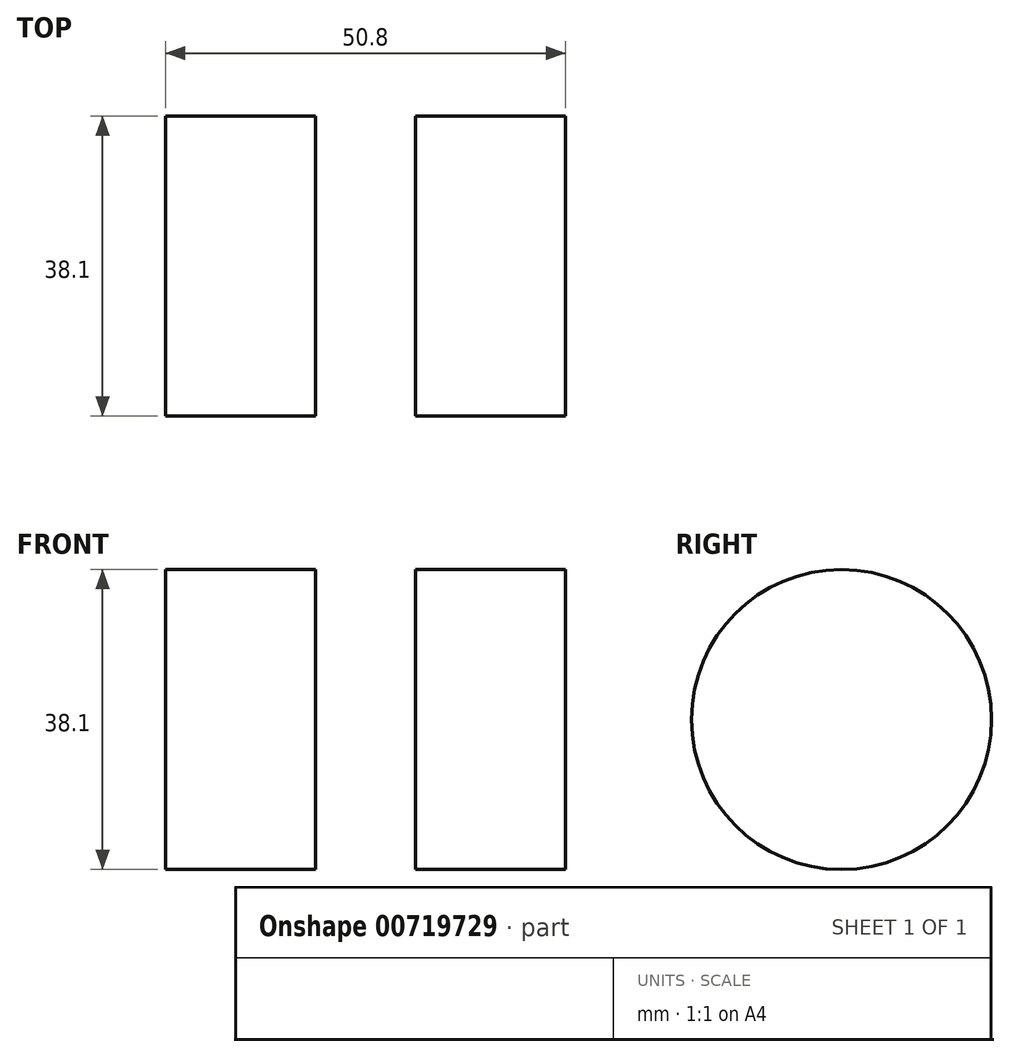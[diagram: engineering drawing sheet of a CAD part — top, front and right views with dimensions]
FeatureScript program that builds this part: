
annotation { "Feature Type Name" : "Feature", "Feature Type Description" : "" }
export const myFeature = defineFeature(function(context is Context, id is Id, definition is map)
    precondition{}
    {
        {
            var Q0;
            Q0=qCreatedBy(makeId("Front.planeOp"),FACE);
            var sketch = newSketch(context, id + "F0", { "sketchPlane" : qUnion([Q0])});
            skLineSegment(sketch, "E0.bottom", {"start": v(0, 0) * mm, "end": v(50.8, 0) * mm});
            skLineSegment(sketch, "E0.top", {"start": v(0, 25.4) * mm, "end": v(50.8, 25.4) * mm});
            skLineSegment(sketch, "E0.left", {"start": v(0, 0) * mm, "end": v(0, 25.4) * mm});
            skLineSegment(sketch, "E0.right", {"start": v(50.8, 0) * mm, "end": v(50.8, 25.4) * mm});
            skSolve(sketch);
        }
        {
            var Q0;
            Q0=makeQuery(id+"F0.imprint","IMPRINT",FACE,{"disambiguationData":[TD([[makeQuery(id+"F0.imprint","IMPRINT",EDGE,{"derivedFrom":sQuery(id+"F0.wireOp",EDGE,"E0.bottom")}),1.0]])]});
            extrude(context, id + "F1", {"entities" : qUnion([Q0]), "depth" : 1778 * mm, "offsetDistance" : 25.4 * mm});
        }
        {
            var Q0;
            Q0=makeQuery(id+"F1.opExtrude","SWEPT_FACE",FACE,{"disambiguationData":[OSD([sQuery(id+"F0.wireOp",EDGE,"E0.right")])]});
            cPlane(context, id + "F2", {"entities" : qUnion([Q0]), "cplaneType" : CPlaneType.OFFSET, "offset" : 19.05 * mm, "oppositeDirection" : true, "width" : 152.4 * mm, "height" : 152.4 * mm});
        }
        {
            var Q0;
            Q0=makeQuery(id+"F1.opExtrude","CAP_FACE",FACE,{"disambiguationData":[OSD([sQuery(id+"F0.wireOp",EDGE,"E0.bottom"),sQuery(id+"F0.wireOp",EDGE,"E0.top"),sQuery(id+"F0.wireOp",EDGE,"E0.left"),sQuery(id+"F0.wireOp",EDGE,"E0.right")])],"isStart":false});
            cPlane(context, id + "F3", {"entities" : qUnion([Q0]), "cplaneType" : CPlaneType.OFFSET, "offset" : 889 * mm, "oppositeDirection" : true, "width" : 152.4 * mm, "height" : 152.4 * mm});
        }
        {
            var Q0;
            Q0=qCreatedBy(id+"F2.planeOp",FACE);
            var sketch = newSketch(context, id + "F4", { "sketchPlane" : qUnion([Q0])});
            skPoint(sketch, "E1", {"position": v(-1791.81, 12.7) * mm});
            skCircle(sketch, "E2", {"center": v(-1791.81, 12.7) * mm, "radius": 22.23 * mm, "construction": true});
            skPoint(sketch, "E3", {"position": v(-1773.58, 25.4) * mm});
            skCircle(sketch, "E4", {"center": v(-1791.81, 12.7) * mm, "radius": 22.23 * mm});
            skCircle(sketch, "E5.MirrorC", {"center": v(13.81, 12.7) * mm, "radius": 22.23 * mm, "construction": true});
            skCircle(sketch, "E6", {"center": v(13.81, 12.7) * mm, "radius": 22.23 * mm});
            skPoint(sketch, "E7", {"position": v(-4.42, 25.4) * mm});
            skSolve(sketch);
        }
        {
            var Q0;
            Q0=makeQuery(id+"F1.opExtrude","SWEPT_FACE",FACE,{"disambiguationData":[OSD([sQuery(id+"F0.wireOp",EDGE,"E0.right")])]});
            var sketch = newSketch(context, id + "F5", { "sketchPlane" : qUnion([Q0])});
            skPoint(sketch, "E8", {"position": v(-1791.81, 12.7) * mm});
            skCircle(sketch, "E9", {"center": v(-1791.81, 12.7) * mm, "radius": 22.23 * mm});
            skCircle(sketch, "E10.MirrorC", {"center": v(13.81, 12.7) * mm, "radius": 22.23 * mm});
            skCircle(sketch, "E11", {"center": v(-1791.81, 12.7) * mm, "radius": 19.05 * mm});
            skSolve(sketch);
        }
        {
            var Q0;
            {var subQ1=sQuery(id+"F0.wireOp",EDGE,"E0.right");var subQ6=makeQuery(id+"F1.opExtrude","CAP_EDGE",EDGE,{"disambiguationData":[OSD([subQ1])],"isStart":true});Q0=makeQuery(id+"F5.imprint","IMPRINT",FACE,{"disambiguationData":[TD([[makeQuery(id+"F5.imprint","IMPRINT",EDGE,{"derivedFrom":subQ6}),-1.0]])]});}
            var Q1;
            {var subQ0=sQuery(id+"F5.wireOp",EDGE,"E9");var subQ1=sQuery(id+"F0.wireOp",EDGE,"E0.right");var subQ2=makeQuery(id+"F1.opExtrude","SWEPT_EDGE",EDGE,{"disambiguationData":[OSD([sQuery(id+"F0.wireOp",EDGE,"E0.bottom"),subQ1])]});var subQ3=makeQuery(id+"F5.imprint","INTERSECT",VERTEX,{"derivedFrom":[subQ2,subQ0]});Q1=makeQuery(id+"F5.imprint","IMPRINT",FACE,{"disambiguationData":[TD([[makeQuery(id+"F5.imprint","IMPRINT",EDGE,{"disambiguationData":[TD([[subQ3,1.0]])],"derivedFrom":subQ0}),1.0]])]});}
            extrude(context, id + "F6", {"entities" : qUnion([Q0, Q1]), "operationType" : NewBodyOperationType.ADD, "oppositeDirection" : true, "depth" : 50.8 * mm, "offsetDistance" : 25.4 * mm});
        }
        {
            var Q0;
            Q0 = qSketchRegion(id + "F4", true);
            extrude(context, id + "F7", {"entities" : qUnion([Q0]), "operationType" : NewBodyOperationType.REMOVE, "oppositeDirection" : true, "depth" : 12.7 * mm, "offsetDistance" : 25.4 * mm});
        }
        {
            var Q0;
            {var subQ0=sQuery(id+"F0.wireOp",EDGE,"E0.right");var subQ1=sQuery(id+"F0.wireOp",EDGE,"E0.top");var subQ2=sQuery(id+"F0.wireOp",EDGE,"E0.bottom");Q0=makeQuery(id+"F6.boolean.opBoolean","MERGE",FACE,{"derivedFrom":[makeQuery(id+"F1.opExtrude","SWEPT_FACE",FACE,{"disambiguationData":[OSD([subQ0])]}),makeQuery(id+"F6.opExtrude","CAP_FACE",FACE,{"disambiguationData":[OSD([subQ2,subQ1,subQ0,sQuery(id+"F5.wireOp",EDGE,"E9"),sQuery(id+"F5.wireOp",EDGE,"E11")])],"isStart":true}),makeQuery(id+"F6.opExtrude","CAP_FACE",FACE,{"disambiguationData":[OSD([subQ2,subQ1,subQ0,sQuery(id+"F5.wireOp",EDGE,"E10.MirrorC")])],"isStart":true})]});}
            var sketch = newSketch(context, id + "F8", { "sketchPlane" : qUnion([Q0])});
            skCircle(sketch, "E12", {"center": v(-1791.81, 12.7) * mm, "radius": 19.05 * mm});
            skCircle(sketch, "E13.MirrorC", {"center": v(13.81, 12.7) * mm, "radius": 19.05 * mm});
            skSolve(sketch);
        }
        {
            var Q0;
            {var subQ2=sQuery(id+"F0.wireOp",EDGE,"E0.right");Q0=makeQuery(id+"F8.imprint","IMPRINT",FACE,{"disambiguationData":[TD([[makeQuery(id+"F8.imprint","IMPRINT",EDGE,{"derivedFrom":makeQuery(id+"F1.opExtrude","CAP_EDGE",EDGE,{"disambiguationData":[OSD([subQ2])],"isStart":false})}),-1.0]])]});}
            var Q1;
            Q1=makeQuery(id+"F8.imprint","IMPRINT",FACE,{"disambiguationData":[TD([[makeQuery(id+"F8.imprint","IMPRINT",EDGE,{"derivedFrom":sQuery(id+"F8.wireOp",EDGE,"E13.MirrorC")}),-1.0]])]});
            extrude(context, id + "F9", {"entities" : qUnion([Q0, Q1]), "operationType" : NewBodyOperationType.REMOVE, "oppositeDirection" : true, "depth" : 50.8 * mm, "offsetDistance" : 25.4 * mm});
        }
    });
